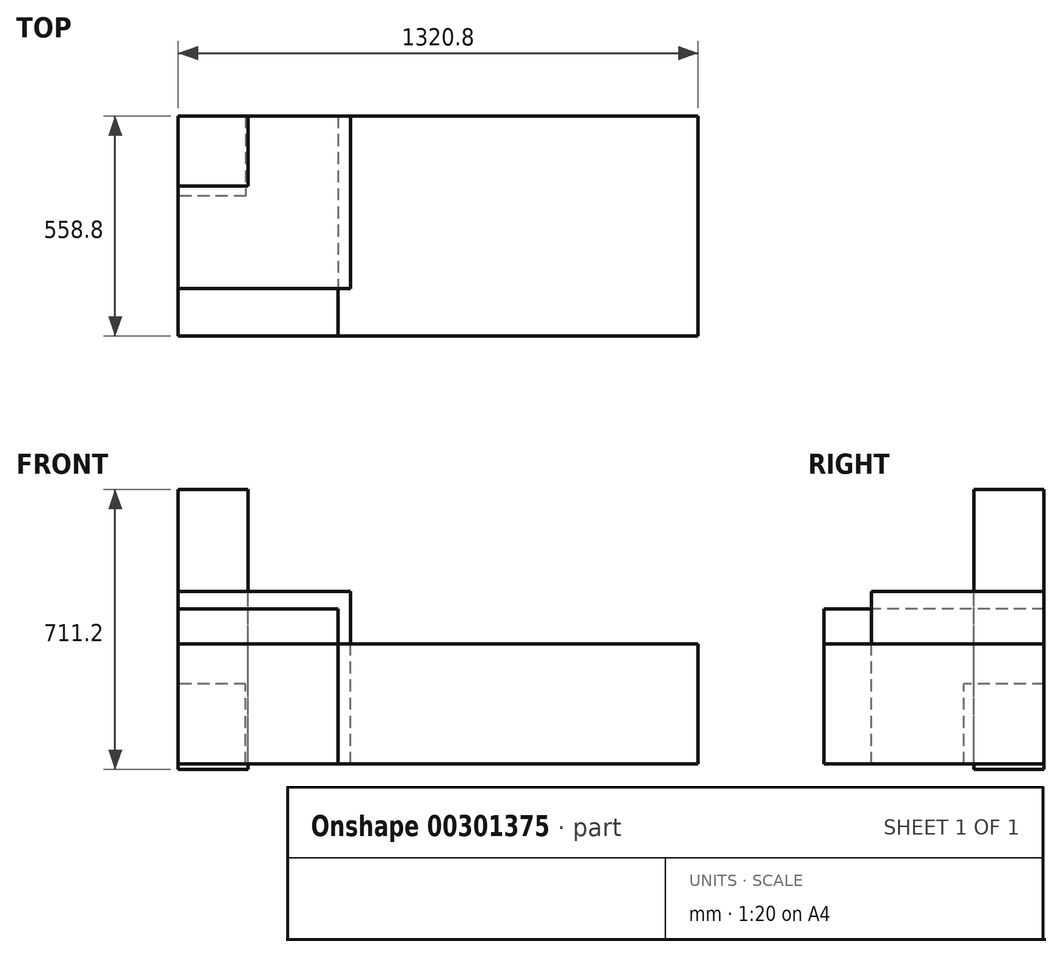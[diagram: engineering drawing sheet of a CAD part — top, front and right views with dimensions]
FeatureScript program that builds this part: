
annotation { "Feature Type Name" : "Feature", "Feature Type Description" : "" }
export const myFeature = defineFeature(function(context is Context, id is Id, definition is map)
    precondition{}
    {
        {
            var Q0;
            Q0=qCreatedBy(makeId("Right.planeOp"),FACE);
            var sketch = newSketch(context, id + "F0", { "sketchPlane" : qUnion([Q0])});
            skLineSegment(sketch, "E0.bottom", {"start": v(0, 0) * mm, "end": v(-558.8, 0) * mm});
            skLineSegment(sketch, "E0.top", {"start": v(0, 393.7) * mm, "end": v(-558.8, 393.7) * mm});
            skLineSegment(sketch, "E0.left", {"start": v(0, 0) * mm, "end": v(0, 393.7) * mm});
            skLineSegment(sketch, "E0.right", {"start": v(-558.8, 0) * mm, "end": v(-558.8, 393.7) * mm});
            skSolve(sketch);
        }
        {
            var Q0;
            Q0 = qSketchRegion(id + "F0", true);
            extrude(context, id + "F1", {"entities" : qUnion([Q0]), "depth" : 406.4 * mm});
        }
        {
            var Q0;
            Q0=qCreatedBy(makeId("Right.planeOp"),FACE);
            var sketch = newSketch(context, id + "F2", { "sketchPlane" : qUnion([Q0])});
            skLineSegment(sketch, "E1.bottom", {"start": v(0, 0) * mm, "end": v(-558.8, 0) * mm});
            skLineSegment(sketch, "E1.top", {"start": v(0, 304.8) * mm, "end": v(-558.8, 304.8) * mm});
            skLineSegment(sketch, "E1.left", {"start": v(0, 0) * mm, "end": v(0, 304.8) * mm});
            skLineSegment(sketch, "E1.right", {"start": v(-558.8, 0) * mm, "end": v(-558.8, 304.8) * mm});
            skSolve(sketch);
        }
        {
            var Q0;
            Q0 = qSketchRegion(id + "F2", true);
            extrude(context, id + "F3", {"entities" : qUnion([Q0]), "depth" : 1320.8 * mm});
        }
        {
            var Q0;
            Q0=qCreatedBy(makeId("Right.planeOp"),FACE);
            var sketch = newSketch(context, id + "F4", { "sketchPlane" : qUnion([Q0])});
            skLineSegment(sketch, "E2.bottom", {"start": v(0, -14.13) * mm, "end": v(-177.8, -14.13) * mm});
            skLineSegment(sketch, "E2.top", {"start": v(0, 697.07) * mm, "end": v(-177.8, 697.07) * mm});
            skLineSegment(sketch, "E2.left", {"start": v(0, -14.13) * mm, "end": v(0, 697.07) * mm});
            skLineSegment(sketch, "E2.right", {"start": v(-177.8, -14.13) * mm, "end": v(-177.8, 697.07) * mm});
            skSolve(sketch);
        }
        {
            var Q0;
            Q0 = qSketchRegion(id + "F4", true);
            extrude(context, id + "F5", {"entities" : qUnion([Q0]), "depth" : 177.8 * mm});
        }
        {
            var Q0;
            Q0=qCreatedBy(makeId("Right.planeOp"),FACE);
            var sketch = newSketch(context, id + "F6", { "sketchPlane" : qUnion([Q0])});
            skLineSegment(sketch, "E3.bottom", {"start": v(0, 0) * mm, "end": v(-438.15, 0) * mm});
            skLineSegment(sketch, "E3.top", {"start": v(0, 438.15) * mm, "end": v(-438.15, 438.15) * mm});
            skLineSegment(sketch, "E3.left", {"start": v(0, 0) * mm, "end": v(0, 438.15) * mm});
            skLineSegment(sketch, "E3.right", {"start": v(-438.15, 0) * mm, "end": v(-438.15, 438.15) * mm});
            skSolve(sketch);
        }
        {
            var Q0;
            Q0 = qSketchRegion(id + "F6", true);
            extrude(context, id + "F7", {"entities" : qUnion([Q0]), "depth" : 438.15 * mm});
        }
        {
            var Q0;
            Q0=qCreatedBy(makeId("Right.planeOp"),FACE);
            var sketch = newSketch(context, id + "F8", { "sketchPlane" : qUnion([Q0])});
            skLineSegment(sketch, "E4.bottom", {"start": v(0, 0) * mm, "end": v(-203.2, 0) * mm});
            skLineSegment(sketch, "E4.top", {"start": v(0, 203.2) * mm, "end": v(-203.2, 203.2) * mm});
            skLineSegment(sketch, "E4.left", {"start": v(0, 0) * mm, "end": v(0, 203.2) * mm});
            skLineSegment(sketch, "E4.right", {"start": v(-203.2, 0) * mm, "end": v(-203.2, 203.2) * mm});
            skSolve(sketch);
        }
        {
            var Q0;
            Q0 = qSketchRegion(id + "F8", true);
            extrude(context, id + "F9", {"entities" : qUnion([Q0]), "depth" : 171.45 * mm});
        }
    });
